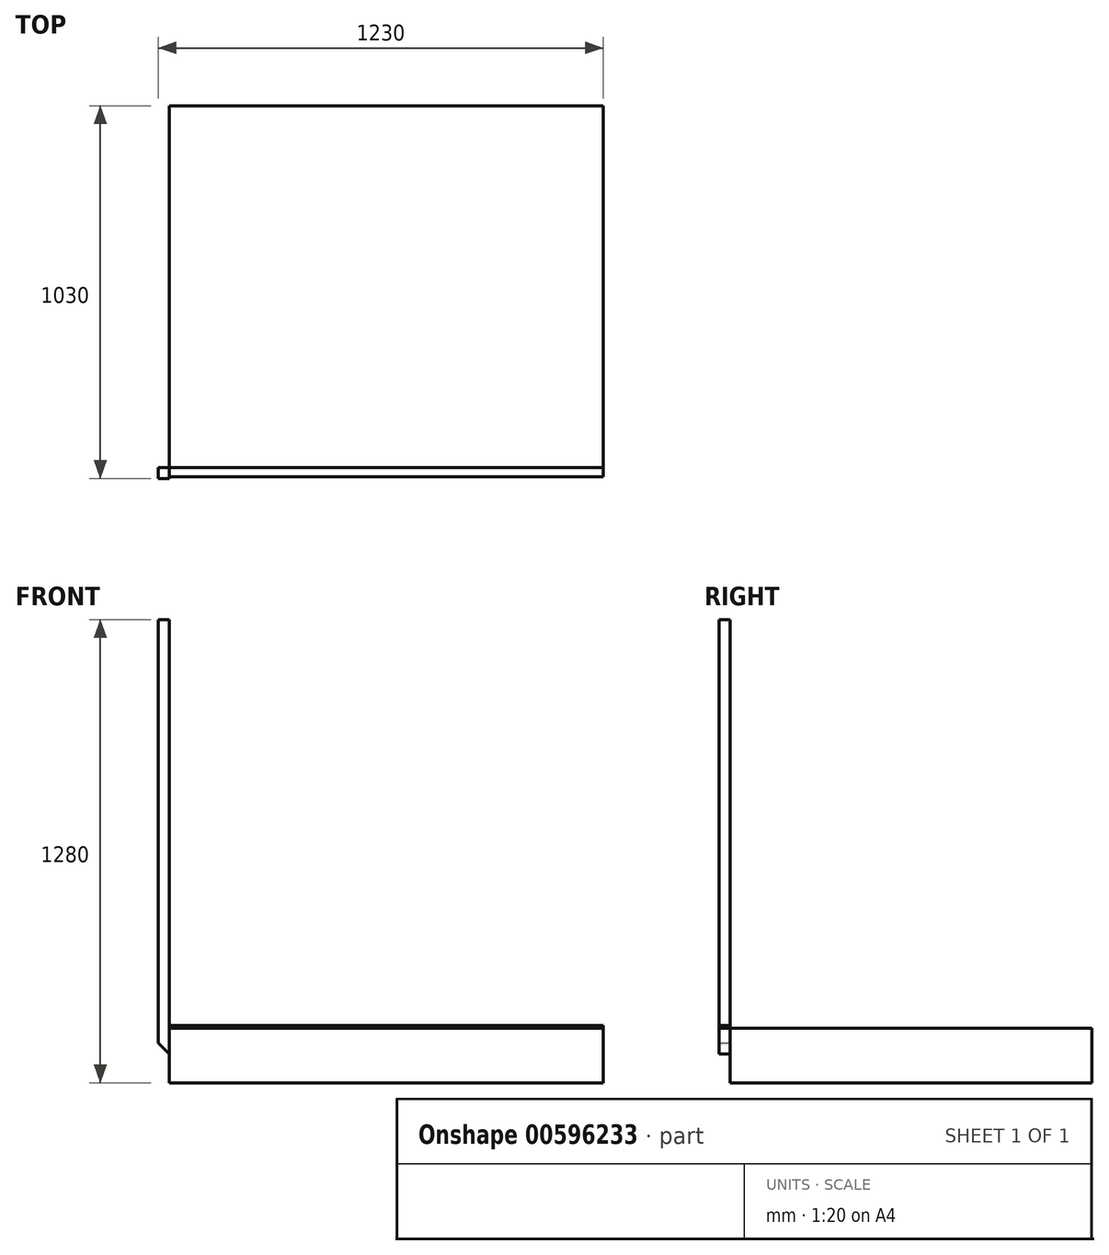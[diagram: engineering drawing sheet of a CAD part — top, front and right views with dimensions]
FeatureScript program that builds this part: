
annotation { "Feature Type Name" : "Feature", "Feature Type Description" : "" }
export const myFeature = defineFeature(function(context is Context, id is Id, definition is map)
    precondition{}
    {
        {
            var Q0;
            Q0=qCreatedBy(makeId("Front.planeOp"),FACE);
            var sketch = newSketch(context, id + "F0", { "sketchPlane" : qUnion([Q0])});
            skLineSegment(sketch, "E0.bottom", {"start": v(-1165.96, 152.73) * mm, "end": v(34.04, 152.73) * mm});
            skLineSegment(sketch, "E0.top", {"start": v(-1165.96, 2.73) * mm, "end": v(34.04, 2.73) * mm});
            skLineSegment(sketch, "E0.left", {"start": v(-1165.96, 152.73) * mm, "end": v(-1165.96, 2.73) * mm});
            skLineSegment(sketch, "E0.right", {"start": v(34.04, 152.73) * mm, "end": v(34.04, 2.73) * mm});
            skSolve(sketch);
        }
        {
            var Q0;
            Q0 = qSketchRegion(id + "F0", true);
            extrude(context, id + "F1", {"entities" : qUnion([Q0]), "depth" : 1000 * mm, "offsetDistance" : 25 * mm});
        }
        {
            var Q0;
            Q0=makeQuery(id+"F1.opExtrude","SWEPT_FACE",FACE,{"disambiguationData":[OSD([sQuery(id+"F0.wireOp",EDGE,"E0.bottom")])]});
            var sketch = newSketch(context, id + "F2", { "sketchPlane" : qUnion([Q0])});
            skLineSegment(sketch, "E1", {"start": v(-1165.96, -1000) * mm, "end": v(-1165.96, -900) * mm});
            skLineSegment(sketch, "E2", {"start": v(-1165.96, -900) * mm, "end": v(-1165.96, -600) * mm});
            skLineSegment(sketch, "E3", {"start": v(-1165.96, -600) * mm, "end": v(-1165.96, -400) * mm});
            skLineSegment(sketch, "E4", {"start": v(-1165.96, -400) * mm, "end": v(-1165.96, -100) * mm});
            skSolve(sketch);
        }
        {
            var Q0;
            Q0=makeQuery(id+"F1.opExtrude","CAP_FACE",FACE,{"disambiguationData":[OSD([sQuery(id+"F0.wireOp",EDGE,"E0.bottom"),sQuery(id+"F0.wireOp",EDGE,"E0.top"),sQuery(id+"F0.wireOp",EDGE,"E0.left"),sQuery(id+"F0.wireOp",EDGE,"E0.right")])],"isStart":false});
            var sketch = newSketch(context, id + "F3", { "sketchPlane" : qUnion([Q0])});
            skLineSegment(sketch, "E5.bottom", {"start": v(-1165.96, 152.73) * mm, "end": v(34.04, 152.73) * mm});
            skLineSegment(sketch, "E5.top", {"start": v(-1165.96, 160.73) * mm, "end": v(34.04, 160.73) * mm});
            skLineSegment(sketch, "E5.left", {"start": v(-1165.96, 152.73) * mm, "end": v(-1165.96, 160.73) * mm});
            skLineSegment(sketch, "E5.right", {"start": v(34.04, 152.73) * mm, "end": v(34.04, 160.73) * mm});
            skSolve(sketch);
        }
        {
            var Q0;
            Q0=makeQuery(id+"F3.imprint","IMPRINT",FACE,{"disambiguationData":[TD([[makeQuery(id+"F3.imprint","IMPRINT",EDGE,{"derivedFrom":sQuery(id+"F3.wireOp",EDGE,"E5.bottom")}),1.0]])]});
            extrude(context, id + "F4", {"entities" : qUnion([Q0]), "depth" : 25 * mm, "offsetDistance" : 25 * mm});
        }
        {
            var Q0;
            Q0=makeQuery(id+"F1.opExtrude","CAP_FACE",FACE,{"disambiguationData":[OSD([sQuery(id+"F0.wireOp",EDGE,"E0.bottom"),sQuery(id+"F0.wireOp",EDGE,"E0.top"),sQuery(id+"F0.wireOp",EDGE,"E0.left"),sQuery(id+"F0.wireOp",EDGE,"E0.right")])],"isStart":false});
            var sketch = newSketch(context, id + "F5", { "sketchPlane" : qUnion([Q0])});
            skLineSegment(sketch, "E6.bottom", {"start": v(-1165.96, 152.73) * mm, "end": v(-1195.96, 152.73) * mm, "construction": true});
            skLineSegment(sketch, "E6.top", {"start": v(-1165.96, 82.73) * mm, "end": v(-1195.96, 82.73) * mm, "construction": true});
            skLineSegment(sketch, "E6.left", {"start": v(-1165.96, 152.73) * mm, "end": v(-1165.96, 82.73) * mm, "construction": true});
            skLineSegment(sketch, "E6.right", {"start": v(-1195.96, 152.73) * mm, "end": v(-1195.96, 82.73) * mm, "construction": true});
            skLineSegment(sketch, "E7.top", {"start": v(-1165.96, 112.73) * mm, "end": v(-1195.96, 112.73) * mm, "construction": true});
            skLineSegment(sketch, "E7.left", {"start": v(-1165.96, 152.73) * mm, "end": v(-1165.96, 112.73) * mm, "construction": true});
            skLineSegment(sketch, "E7.right", {"start": v(-1195.96, 152.73) * mm, "end": v(-1195.96, 112.73) * mm, "construction": true});
            skLineSegment(sketch, "E8.top", {"start": v(-1165.96, 1282.73) * mm, "end": v(-1195.96, 1282.73) * mm, "construction": true});
            skLineSegment(sketch, "E8.left", {"start": v(-1165.96, 82.73) * mm, "end": v(-1165.96, 1282.73) * mm, "construction": true});
            skLineSegment(sketch, "E8.right", {"start": v(-1195.96, 82.73) * mm, "end": v(-1195.96, 1282.73) * mm, "construction": true});
            skSolve(sketch);
        }
        {
            var Q0;
            Q0=makeQuery(id+"F5.imprint","IMPRINT",FACE,{"disambiguationData":[TD([[makeQuery(id+"F5.imprint","IMPRINT",EDGE,{"derivedFrom":makeQuery(id+"F1.opExtrude","CAP_EDGE",EDGE,{"disambiguationData":[OSD([sQuery(id+"F0.wireOp",EDGE,"E0.bottom")])],"isStart":false})}),-1.0]])]});
            var sketch = newSketch(context, id + "F6", { "sketchPlane" : qUnion([Q0])});
            skLineSegment(sketch, "E9.0", {"start": v(-1165.96, 1282.73) * mm, "end": v(-1195.96, 1282.73) * mm});
            skLineSegment(sketch, "E9.1", {"start": v(-1165.96, 82.73) * mm, "end": v(-1165.96, 1282.73) * mm});
            skLineSegment(sketch, "E9.2", {"start": v(-1195.96, 112.73) * mm, "end": v(-1195.96, 1282.73) * mm});
            skLineSegment(sketch, "E9.7", {"start": v(-1195.96, 152.73) * mm, "end": v(-1195.96, 112.73) * mm});
            skLineSegment(sketch, "E9.9", {"start": v(-1165.96, 152.73) * mm, "end": v(-1165.96, 82.73) * mm});
            skPoint(sketch, "E9.6.start.orphan", {"position": v(-1165.96, 82.73) * mm});
            skPoint(sketch, "E9.5.end.orphan", {"position": v(-1195.96, 112.73) * mm});
            skPoint(sketch, "E9.5.start.orphan", {"position": v(-1165.96, 112.73) * mm});
            skPoint(sketch, "E9.4.start.orphan", {"position": v(-1165.96, 82.73) * mm});
            skPoint(sketch, "E9.8.end.orphan", {"position": v(-1195.96, 152.73) * mm});
            skPoint(sketch, "E9.8.start.orphan", {"position": v(-1165.96, 152.73) * mm});
            skPoint(sketch, "E9.3.end.orphan", {"position": v(-1195.96, 152.73) * mm});
            skPoint(sketch, "E9.3.start.orphan", {"position": v(-1165.96, 152.73) * mm});
            skLineSegment(sketch, "E10", {"start": v(-1195.96, 112.73) * mm, "end": v(-1165.96, 82.73) * mm});
            skSolve(sketch);
        }
        {
            var Q0;
            Q0 = qSketchRegion(id + "F6", true);
            extrude(context, id + "F7", {"entities" : qUnion([Q0]), "operationType" : NewBodyOperationType.ADD, "depth" : 30 * mm, "offsetDistance" : 25 * mm});
        }
    });
